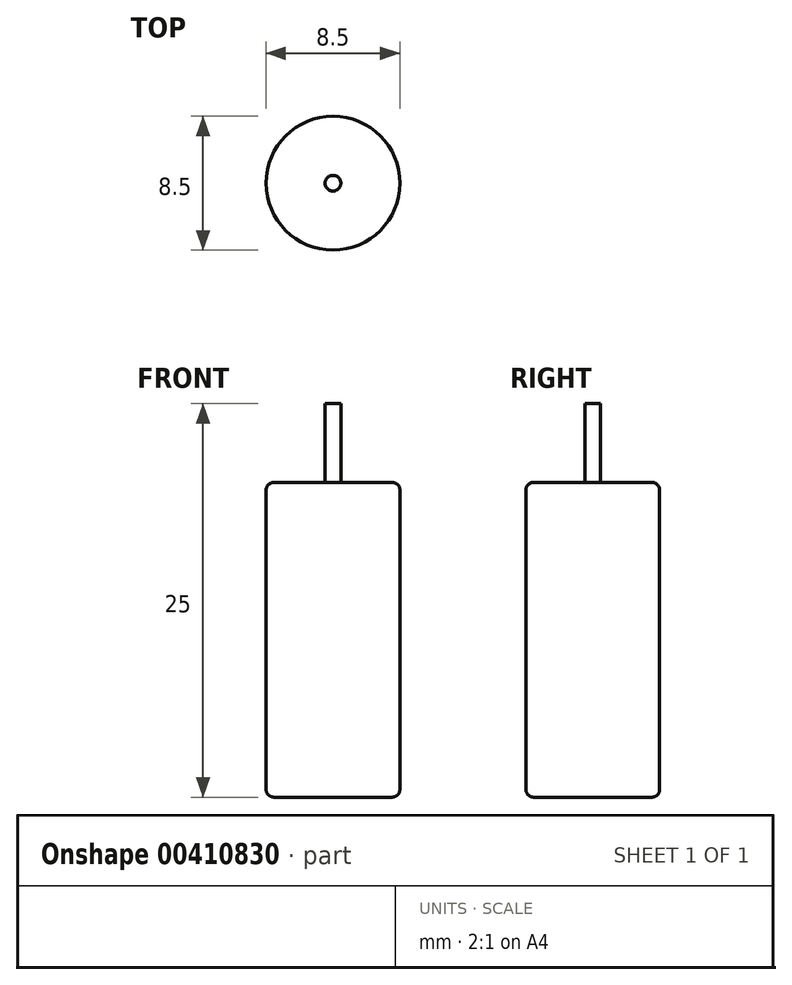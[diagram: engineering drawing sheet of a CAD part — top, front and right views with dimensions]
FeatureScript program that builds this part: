
annotation { "Feature Type Name" : "Feature", "Feature Type Description" : "" }
export const myFeature = defineFeature(function(context is Context, id is Id, definition is map)
    precondition{}
    {
        {
            var Q0;
            Q0=qCreatedBy(makeId("Top.planeOp"),FACE);
            var sketch = newSketch(context, id + "F0", { "sketchPlane" : qUnion([Q0])});
            skCircle(sketch, "E0", {"center": v(0, 0) * mm, "radius": 4.25 * mm});
            skSolve(sketch);
        }
        {
            var Q0;
            Q0 = qSketchRegion(id + "F0", true);
            extrude(context, id + "F1", {"entities" : qUnion([Q0]), "depth" : 20 * mm});
        }
        {
            var Q0;
            Q0=makeQuery(id+"F1.opExtrude","CAP_EDGE",EDGE,{"disambiguationData":[OSD([sQuery(id+"F0.wireOp",EDGE,"E0")])],"isStart":false});
            fillet(context, id + "F2", {"entities" : qUnion([Q0]), "radius" : .5 * mm, "tangentPropagation" : true, "allowEdgeOverflow" : false});
        }
        {
            var Q0;
            Q0=makeQuery(id+"F1.opExtrude","CAP_EDGE",EDGE,{"disambiguationData":[OSD([sQuery(id+"F0.wireOp",EDGE,"E0")])],"isStart":true});
            fillet(context, id + "F3", {"entities" : qUnion([Q0]), "radius" : .5 * mm, "tangentPropagation" : true, "allowEdgeOverflow" : false});
        }
        {
            var Q0;
            Q0=makeQuery(id+"F1.opExtrude","CAP_FACE",FACE,{"disambiguationData":[OSD([sQuery(id+"F0.wireOp",EDGE,"E0")])],"isStart":false});
            var sketch = newSketch(context, id + "F4", { "sketchPlane" : qUnion([Q0])});
            skCircle(sketch, "E1", {"center": v(0, 0) * mm, "radius": 0.5 * mm});
            skSolve(sketch);
        }
        {
            var Q0;
            Q0 = qSketchRegion(id + "F4", true);
            extrude(context, id + "F5", {"entities" : qUnion([Q0]), "operationType" : NewBodyOperationType.ADD, "depth" : 5 * mm});
        }
    });
